# Revit family: 19133 Велопарковка «Рапид» Хоббика
name_source: partatom
category: Антураж
revit_build: Autodesk Revit 2018 (Build: 20180423_1000(x64)
units: mm (PartAtom-declared; Revit-internal decimal feet)

## family parameters
Всегда вертикально = Да
Источник визуального образа = Геометрия семейства
На основе рабочей плоскости = Нет
Общий = Нет
При загрузке вырезать с полостями = Нет
Точка расчета площади = Нет

## types (2) — shared parameters
URL = https://hobbyka.ru
Артикул товара = Арт. 19133
Высота = 420 мм
Группа модели = Велопарковки
Изготовитель = ООО «Хоббика»
Материал изделия = Сталь
Цвет каркаса = Сталь
Ширина = 570 мм

## per-type parameters (varying)
| type | Версия 2 места | Версия 3 места | Длина | Изображение типоразмера | Описание |
| Версия 2 места | Да | Нет | 580 мм | Велопарковка «Рапид» Арт 19133 2 места.jpeg | Велопарковка «Рапид». Версия на 2 места |
| Версия 3 места | Нет | Да | 1000 мм | Велопарковка «Рапид» Арт 19133 3 места.jpeg | Велопарковка «Рапид». Версия на 3 места |
